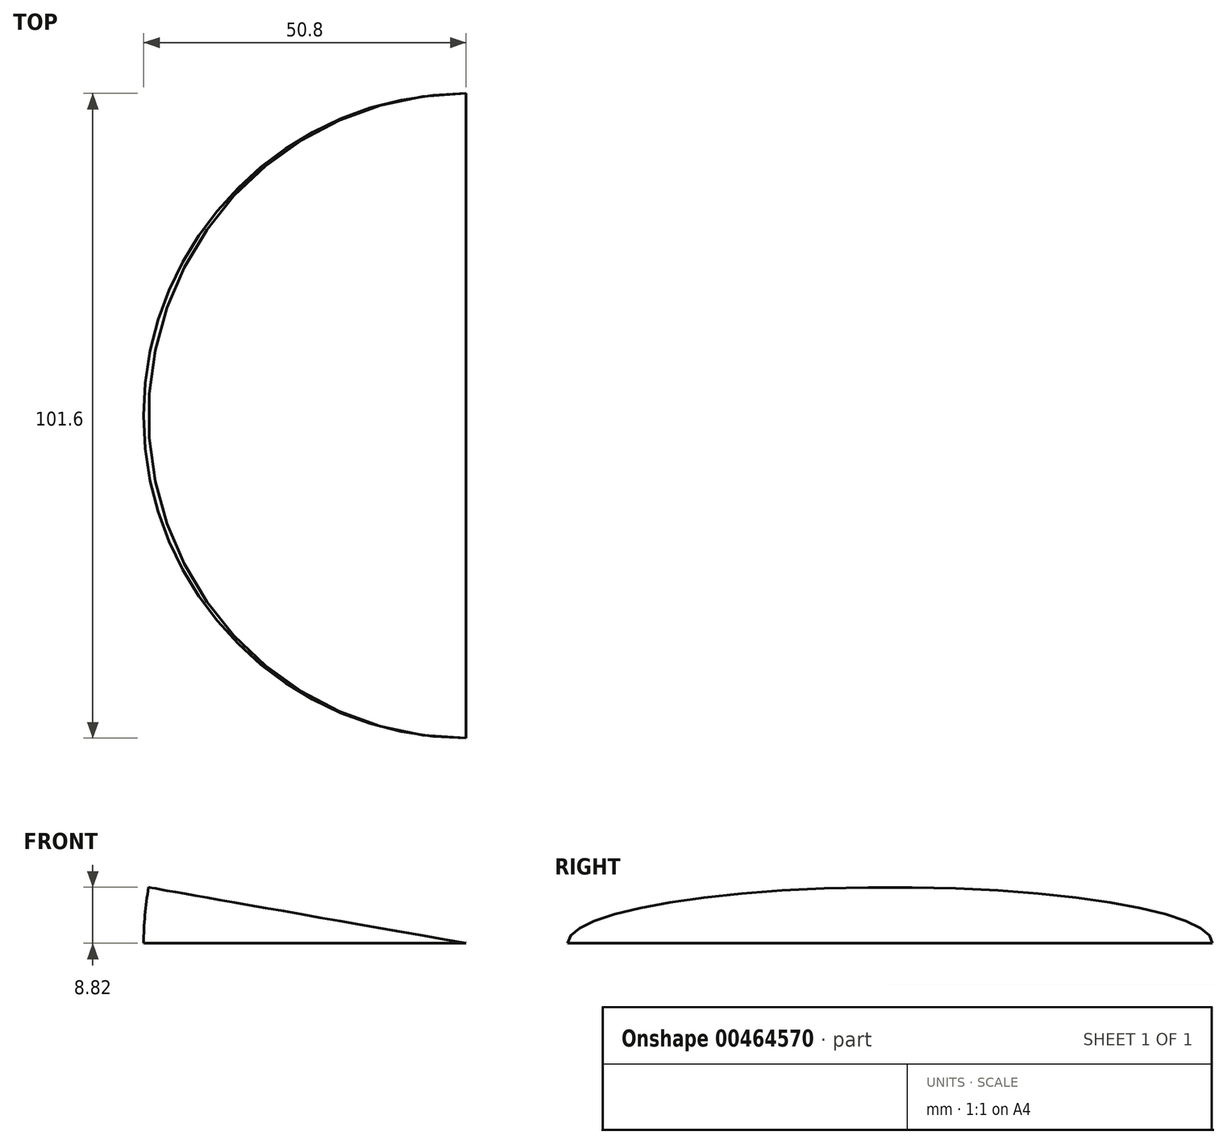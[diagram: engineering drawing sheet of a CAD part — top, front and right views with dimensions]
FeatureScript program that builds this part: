
annotation { "Feature Type Name" : "Feature", "Feature Type Description" : "" }
export const myFeature = defineFeature(function(context is Context, id is Id, definition is map)
    precondition{}
    {
        {
            var Q0;
            Q0=qCreatedBy(makeId("Top.planeOp"),FACE);
            var sketch = newSketch(context, id + "F0", { "sketchPlane" : qUnion([Q0])});
            skArc(sketch, "E0", {"start": v(0, 50.8) * mm, "mid": v(-50.8, 0) * mm, "end": v(0, -50.8) * mm});
            skLineSegment(sketch, "E1", {"start": v(0, 50.8) * mm, "end": v(0, 0) * mm});
            skLineSegment(sketch, "E2", {"start": v(0, 0) * mm, "end": v(0, -50.8) * mm});
            skSolve(sketch);
        }
        {
            var Q0;
            Q0=qCreatedBy(makeId("Top.planeOp"),FACE);
            var sketch = newSketch(context, id + "F1", { "sketchPlane" : qUnion([Q0])});
            skLineSegment(sketch, "E3", {"start": v(0, 0) * mm, "end": v(25.37, 0) * mm});
            skLineSegment(sketch, "E4", {"start": v(0, -26.04) * mm, "end": v(25.37, -26.04) * mm});
            skLineSegment(sketch, "E5", {"start": v(25.37, -26.04) * mm, "end": v(25.37, 0) * mm});
            skLineSegment(sketch, "E6", {"start": v(0, -26.04) * mm, "end": v(0, 0) * mm});
            skSolve(sketch);
        }
        {
            var Q0;
            Q0 = qSketchRegion(id + "F0", true);
            var Q1;
            Q1=sQuery(id+"F0.wireOp",EDGE,"E0");
            var Q2;
            Q2=sQuery(id+"F1.wireOp",EDGE,"E6");
            revolve(context, id + "F2", {"entities" : qUnion([Q0]), "surfaceEntities" : qUnion([Q1]), "axis" : qUnion([Q2]), "revolveType" : RevolveType.ONE_DIRECTION, "angle" : 10 * degree});
        }
        {
            var Q0;
            Q0=makeQuery(id+"F2.opRevolve","CAP_EDGE",EDGE,{"disambiguationData":[OSD([sQuery(id+"F0.wireOp",EDGE,"E0")])],"isStart":false});
            cPoint(context, id + "F3", {"entities" : qUnion([Q0]), "parameter" : 0.5});
        }
        {
            var Q0;
            Q0=sQuery(id+"F0.wireOp",VERTEX,"E0.start");
            var Q1;
            Q1 = qCreatedBy(id + "F3" ,VERTEX);
            var Q2;
            Q2=sQuery(id+"F1.wireOp",VERTEX,"E6.start");
            cPlane(context, id + "F4", {"entities" : qUnion([Q0, Q1, Q2]), "cplaneType" : CPlaneType.THREE_POINT, "offset" : 25.4 * mm, "width" : 152.4 * mm, "height" : 152.4 * mm});
        }
        {
            var Q0;
            Q0=qCreatedBy(id+"F4.planeOp",FACE);
            var sketch = newSketch(context, id + "F5", { "sketchPlane" : qUnion([Q0])});
            skLineSegment(sketch, "E7", {"start": v(0, 0) * mm, "end": v(46.13, 0) * mm});
            skLineSegment(sketch, "E8", {"start": v(0, 50.8) * mm, "end": v(46.13, 50.8) * mm});
            skLineSegment(sketch, "E9", {"start": v(46.13, 50.8) * mm, "end": v(46.13, 0) * mm});
            skLineSegment(sketch, "E10", {"start": v(0, 0) * mm, "end": v(0, 50.8) * mm});
            skSolve(sketch);
        }
        {
            var Q0;
            Q0=makeQuery(id+"F2.opRevolve","CAP_EDGE",EDGE,{"disambiguationData":[OSD([sQuery(id+"F0.wireOp",EDGE,"E0")])],"isStart":false});
            var Q1;
            Q1=sQuery(id+"F0.wireOp",EDGE,"E2");
            revolve(context, id + "F6", {"bodyType" : ToolBodyType.SURFACE, "operationType" : NewBodyOperationType.REMOVE, "surfaceEntities" : qUnion([Q0]), "axis" : qUnion([Q1]), "revolveType" : RevolveType.ONE_DIRECTION, "oppositeDirection" : true, "angle" : 10 * degree});
        }
        {
            var Q0;
            Q0=makeQuery(id+"F5.imprint","IMPRINT",FACE,{"disambiguationData":[TD([[makeQuery(id+"F5.imprint","IMPRINT",EDGE,{"derivedFrom":sQuery(id+"F5.wireOp",EDGE,"E7")}),1.0]])]});
            var Q1;
            Q1=sQuery(id+"F5.wireOp",EDGE,"E7");
            var Q2;
            Q2=sQuery(id+"F5.wireOp",EDGE,"E8");
            var Q3;
            Q3=sQuery(id+"F5.wireOp",EDGE,"E9");
            var Q4;
            Q4=sQuery(id+"F5.wireOp",EDGE,"E10");
            revolve(context, id + "F7", {"bodyType" : ToolBodyType.SURFACE, "entities" : qUnion([Q0]), "surfaceEntities" : qUnion([Q1, Q2, Q3]), "axis" : qUnion([Q4]), "revolveType" : RevolveType.ONE_DIRECTION, "oppositeDirection" : true, "angle" : 10 * degree});
        }
    });
